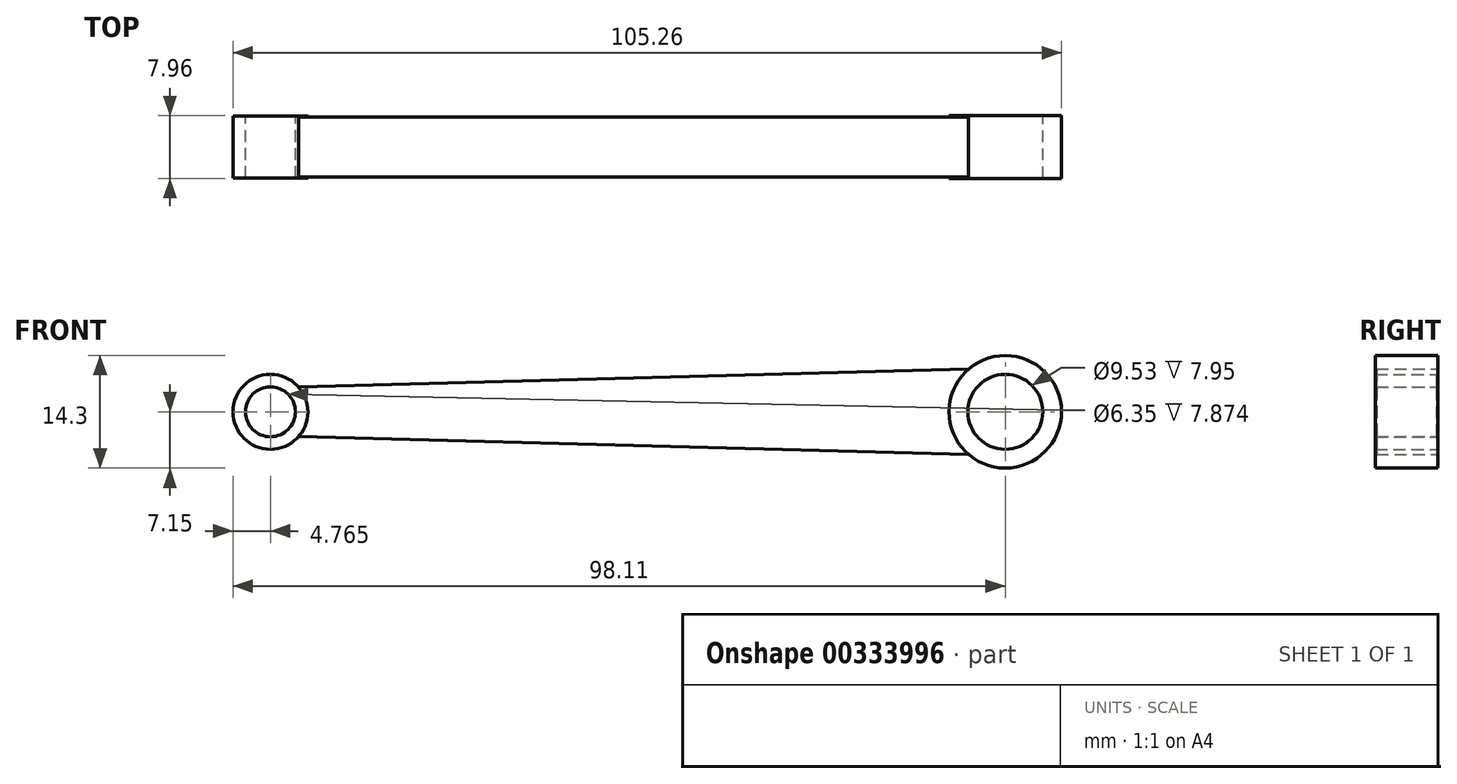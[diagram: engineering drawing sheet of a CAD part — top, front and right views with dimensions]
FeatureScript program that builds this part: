
annotation { "Feature Type Name" : "Feature", "Feature Type Description" : "" }
export const myFeature = defineFeature(function(context is Context, id is Id, definition is map)
    precondition{}
    {
        {
            var Q0;
            Q0=qCreatedBy(makeId("Front.planeOp"),FACE);
            var sketch = newSketch(context, id + "F0", { "sketchPlane" : qUnion([Q0])});
            skArc(sketch, "E0", {"start": v(-89.76, 3.14) * mm, "mid": v(-98.1, 0) * mm, "end": v(-89.76, -3.14) * mm});
            skArc(sketch, "E1", {"start": v(-4.67, -5.41) * mm, "mid": v(7.15, 0) * mm, "end": v(-4.67, 5.41) * mm});
            skCircle(sketch, "E2", {"center": v(-93.35, 0) * mm, "radius": 3.18 * mm});
            skCircle(sketch, "E3", {"center": v(0, 0) * mm, "radius": 4.76 * mm});
            skLineSegment(sketch, "E4", {"start": v(-89.76, 3.14) * mm, "end": v(-4.67, 5.41) * mm});
            skLineSegment(sketch, "E5.MirrorCS", {"start": v(-89.76, -3.14) * mm, "end": v(-4.67, -5.41) * mm});
            skLineSegment(sketch, "E6", {"start": v(-93.35, 0) * mm, "end": v(53.52, 0) * mm, "construction": true});
            skSolve(sketch);
        }
        {
            var Q0;
            Q0=makeQuery(id+"F0.imprint","IMPRINT",FACE,{"disambiguationData":[TD([[makeQuery(id+"F0.imprint","IMPRINT",EDGE,{"derivedFrom":sQuery(id+"F0.wireOp",EDGE,"E0")}),1.0]])]});
            extrude(context, id + "F1", {"entities" : qUnion([Q0]), "endBound" : BoundingType.SYMMETRIC, "depth" : 7.62 * mm});
        }
        {
            var Q0;
            Q0=qCreatedBy(makeId("Front.planeOp"),FACE);
            var sketch = newSketch(context, id + "F2", { "sketchPlane" : qUnion([Q0])});
            skCircle(sketch, "E7.0", {"center": v(0, 0) * mm, "radius": 4.76 * mm});
            skArc(sketch, "E8.0", {"start": v(-4.67, -5.41) * mm, "mid": v(7.15, 0) * mm, "end": v(-4.67, 5.41) * mm});
            skArc(sketch, "E9", {"start": v(-4.67, 5.41) * mm, "mid": v(-7.15, 0) * mm, "end": v(-4.67, -5.41) * mm});
            skSolve(sketch);
        }
        {
            var Q0;
            Q0 = qSketchRegion(id + "F2", true);
            extrude(context, id + "F3", {"entities" : qUnion([Q0]), "operationType" : NewBodyOperationType.ADD, "endBound" : BoundingType.SYMMETRIC, "depth" : 7.95 * mm});
        }
        {
            var Q0;
            Q0=qCreatedBy(makeId("Front.planeOp"),FACE);
            var sketch = newSketch(context, id + "F4", { "sketchPlane" : qUnion([Q0])});
            skCircle(sketch, "E10.0", {"center": v(-93.35, 0) * mm, "radius": 3.18 * mm});
            skArc(sketch, "E11.0", {"start": v(-89.76, 3.14) * mm, "mid": v(-98.1, 0) * mm, "end": v(-89.76, -3.14) * mm});
            skArc(sketch, "E12", {"start": v(-89.76, -3.14) * mm, "mid": v(-88.58, 0) * mm, "end": v(-89.76, 3.14) * mm});
            skSolve(sketch);
        }
        {
            var Q0;
            Q0 = qSketchRegion(id + "F4", true);
            extrude(context, id + "F5", {"entities" : qUnion([Q0]), "operationType" : NewBodyOperationType.ADD, "endBound" : BoundingType.SYMMETRIC, "depth" : 7.87 * mm});
        }
    });
